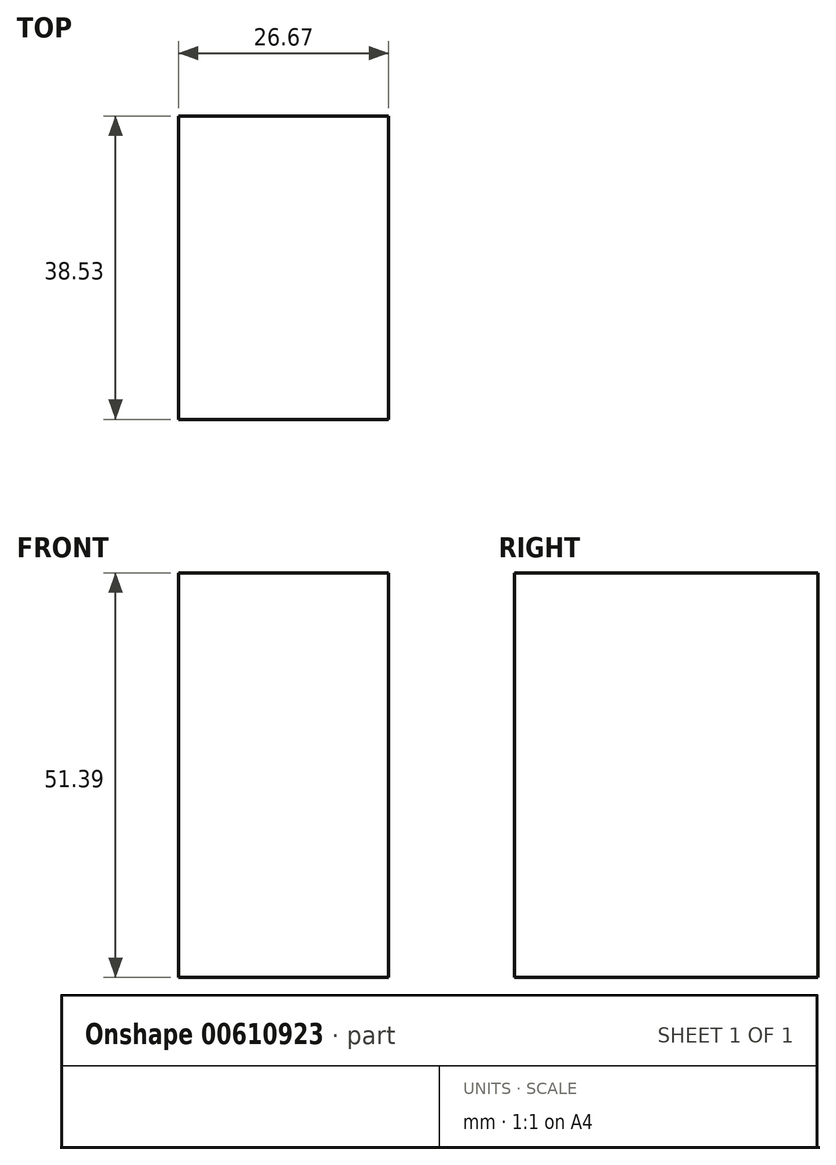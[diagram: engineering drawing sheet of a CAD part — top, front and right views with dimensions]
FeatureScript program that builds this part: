
annotation { "Feature Type Name" : "Feature", "Feature Type Description" : "" }
export const myFeature = defineFeature(function(context is Context, id is Id, definition is map)
    precondition{}
    {
        {
            var Q0;
            Q0=qCreatedBy(makeId("Right.planeOp"),FACE);
            var sketch = newSketch(context, id + "F0", { "sketchPlane" : qUnion([Q0])});
            skLineSegment(sketch, "E0.bottom", {"start": v(128.9, 71.64) * mm, "end": v(167.42, 71.64) * mm});
            skLineSegment(sketch, "E0.top", {"start": v(128.9, 20.25) * mm, "end": v(167.42, 20.25) * mm});
            skLineSegment(sketch, "E0.left", {"start": v(128.9, 71.64) * mm, "end": v(128.9, 20.25) * mm});
            skLineSegment(sketch, "E0.right", {"start": v(167.42, 71.64) * mm, "end": v(167.42, 20.25) * mm});
            skSolve(sketch);
        }
        {
            var Q0;
            Q0=makeQuery(id+"F0.imprint","IMPRINT",FACE,{"disambiguationData":[TD([[makeQuery(id+"F0.imprint","IMPRINT",EDGE,{"derivedFrom":sQuery(id+"F0.wireOp",EDGE,"E0.bottom")}),-1.0]])]});
            extrude(context, id + "F1", {"entities" : qUnion([Q0]), "oppositeDirection" : true, "depth" : 26.67 * mm, "offsetDistance" : 25.4 * mm});
        }
    });
